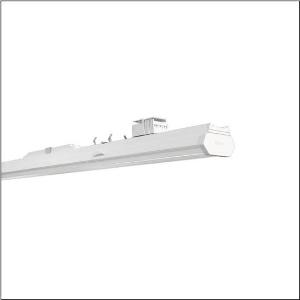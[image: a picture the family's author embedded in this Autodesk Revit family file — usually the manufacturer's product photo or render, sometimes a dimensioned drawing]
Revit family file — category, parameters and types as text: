
# Revit family: licross_r__11_protected_mo_51td12mn4axg_dbc1
name_source: partatom
category: Lighting Fixtures
units: mm (PartAtom-declared; Revit-internal decimal feet)

## family parameters
Cut with Voids When Loaded = No
Host = Face
Light Source = No
Part Type = Normal
Room Calculation Point = No
Round Connector Dimension = Use Diameter
Shared = No

## types (1)
- --- (1 x LED, 10020 lm, 55.3 W, 4000K)
    Apparent Load = 55 VA
    CIE Flux Codes = 73 92 98 99 100
    Color Rendering = 80
    Color Temperature = 4000K
    Default Elevation = 1800 mm
    Description = Licross® 11 Protected MO, luminaire insert, of sheet steel, galvanised, coil coated, white, length: 1.500mm, width: 90mm, height: 101mm, LED rated luminous flux: 10.030lm, light colour: 840, control gear: ON/OFF Multilumen, with plug, 3-pole, with phase selection, mains connection: 220..240V, AC, 50/60Hz, rated input power: 55W, halogen-free wiring, primary light control with lens, of plastic, primary optical cover: cover, of PMMA, light emission: direct distribution, primary light characteristic: symmetric, protection rating (complete): IP54, insulation class (complete): insulation class I (protective earthing), certification: CE, ENEC, VDE, UKCA, protection symbol: D if used in an environment with non-conductive dust loads with corresponding accessories, impact resistance: IK06, permissible ambient temperature for indoor applications: -35..+40°C, corresponds to IFS (International Featured Standards) requirements for safety and quality in the food industry, reducing of maximum allowable ambient temperature of 5°C with ceiling mounting, LABS conformity tested according to VDMA 24364:2018-05, packaging unit: 1 piece
    Height = 92 mm
    Lamp = 1 x LED
    Lamp Light Flux = 10020 lm
    Lamp Power = 55.3 W
    Lamp count = 1
    Length = 1500 mm
    Luminous efficacy = 181 lm/W
    Manufacturer = Siteco
    ModVariant = No
    Model = 51TD12MN4AXG
    Mounting Place = Ceiling
    Mounting Type = Pendant
    Number of Poles = 1
    OnlyDefault = Yes
    Power Factor = 1
    Product Name = Licross® 11 Protected MO
    Product group = luminaire insert
    ProductGroupID = 901
    Protection Class = Protection class I
    Protection Degree = IP 54
    RLX_Detail_Level = 1
    RLX_Emergency_Light_Flux = 0 lm
    RLX_Emergency_Type = 0
    RLX_Emergency_Type_DB = No
    RlxData = <blob elided: 22141 chars, md5=dd64c4dc>
    Socket = socket
    Standby Power = 0 W
    System Light Flux = 10020 lm
    System Power = 55 W
    Type Comments = factory setting: luminous flux: 100 % | (A | C | E) | 126 mA
    Type Image = l_1256145.jpg
    URL = http://relux.com
    VarID = @adj_038125
    Voltage = 0 V
    Weight = 0.00 kg
    Width = 88 mm

## geometry (parser evidence)
native form markers: Blend x4, Sweep x9
no freeform markers — native parametric forms only
